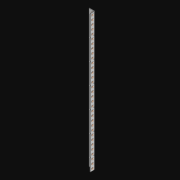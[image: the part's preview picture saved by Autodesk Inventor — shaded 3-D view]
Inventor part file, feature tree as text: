
AUTODESK INVENTOR PART (.ipt)
format: ipt  version: 2021 (Build 250183000, 183)  size: 1,321,984 bytes
history: native  units: in
note: dims shown in document units (in); Inventor stores cm internally (conversion verified against a paired STEP export)
features: extrude x68, other x66, sketch x4, pattern_linear x2, sheet_metal_op x1
ambient origin geometry x8: Origin, YZ Plane, XZ Plane, XY Plane, X Axis, Y Axis, Z Axis, Center Point
bodies: Solid1 (feature_tree)
feature tree (141):
  pattern_linear  "Rectangular Pattern1"  Spacing1=0.5in  [1 undecoded]
  pattern_linear  "Rectangular Pattern3"  Count1=33  [1 undecoded]
  extrude  "Extrusion1"  Depth=0.5in
  extrude  "Extrusion2"  Depth=1.0in
  sketch  "Sketch1"  dims[d0=0.182in]
  other  "Srf1"
  sketch  "Sketch3"  dims[d1=0.063in d2=0.0in]
  other  "Srf3"
  other  "Srf4"
  other  "Srf5"
  other  "Srf6"
  other  "Srf7"
  other  "Srf8"
  other  "Srf9"
  other  "Srf10"
  other  "Srf11"
  other  "Srf12"
  other  "Srf13"
  other  "Srf14"
  other  "Srf15"
  other  "Srf16"
  other  "Srf17"
  other  "Srf18"
  other  "Srf19"
  other  "Srf20"
  other  "Srf21"
  other  "Srf22"
  other  "Srf23"
  other  "Srf24"
  other  "Srf25"
  other  "Srf26"
  other  "Srf27"
  other  "Srf28"
  other  "Srf29"
  other  "Srf30"
  other  "Srf31"
  other  "Srf32"
  other  "Srf33"
  other  "Srf34"
  other  "Srf35"
  other  "Srf142"
  other  "Srf143"
  other  "Srf144"
  other  "Srf145"
  other  "Srf146"
  other  "Srf147"
  other  "Srf148"
  other  "Srf149"
  other  "Srf150"
  other  "Srf151"
  other  "Srf152"
  other  "Srf153"
  other  "Srf154"
  other  "Srf155"
  other  "Srf156"
  other  "Srf157"
  other  "Srf158"
  other  "Srf159"
  other  "Srf160"
  other  "Srf161"
  other  "Srf162"
  other  "Srf163"
  other  "Srf164"
  other  "Srf165"
  other  "Srf166"
  other  "Srf167"
  other  "Srf168"
  other  "Srf169"
  other  "Srf170"
  other  "Srf171"
  other  "Srf172"
  other  "Srf173"
  sketch  "Sketch4"  dims[d6=0.182in]
  sketch  "Sketch5"  dims[d7=0.063in d8=0.0in d11=0.5in d12=0.3937in d14=0.5in d18=12.9921in d20=0.5in d21=1.0in d22=0.0in d23=0.841in d24=0.0in]
  sheet_metal_op  "Fold1"
  extrude  "ExtrusionSrf1"  TaperAngle=0.0deg  [1 undecoded]
  extrude  "ExtrusionSrf3"  Depth=1.0in TaperAngle=0.0deg
  extrude  "ExtrusionSrf4"  [1 undecoded]
  extrude  "ExtrusionSrf5"  [1 undecoded]
  extrude  "ExtrusionSrf6"  [1 undecoded]
  extrude  "ExtrusionSrf7"  [1 undecoded]
  extrude  "ExtrusionSrf8"  [1 undecoded]
  extrude  "ExtrusionSrf9"  [1 undecoded]
  extrude  "ExtrusionSrf10"  [1 undecoded]
  extrude  "ExtrusionSrf11"  [1 undecoded]
  extrude  "ExtrusionSrf12"  [1 undecoded]
  extrude  "ExtrusionSrf13"  [1 undecoded]
  extrude  "ExtrusionSrf14"  [1 undecoded]
  extrude  "ExtrusionSrf15"  [1 undecoded]
  extrude  "ExtrusionSrf16"  [1 undecoded]
  extrude  "ExtrusionSrf17"  [1 undecoded]
  extrude  "ExtrusionSrf18"  [1 undecoded]
  extrude  "ExtrusionSrf19"  [1 undecoded]
  extrude  "ExtrusionSrf20"  [1 undecoded]
  extrude  "ExtrusionSrf21"  [1 undecoded]
  extrude  "ExtrusionSrf22"  [1 undecoded]
  extrude  "ExtrusionSrf23"  [1 undecoded]
  extrude  "ExtrusionSrf24"  [1 undecoded]
  extrude  "ExtrusionSrf25"  [1 undecoded]
  extrude  "ExtrusionSrf26"  [1 undecoded]
  extrude  "ExtrusionSrf27"  [1 undecoded]
  extrude  "ExtrusionSrf28"  [1 undecoded]
  extrude  "ExtrusionSrf29"  [1 undecoded]
  extrude  "ExtrusionSrf30"  [1 undecoded]
  extrude  "ExtrusionSrf31"  [1 undecoded]
  extrude  "ExtrusionSrf32"  [1 undecoded]
  extrude  "ExtrusionSrf33"  [1 undecoded]
  extrude  "ExtrusionSrf34"  [1 undecoded]
  extrude  "ExtrusionSrf35"  [1 undecoded]
  extrude  "ExtrusionSrf142"  [1 undecoded]
  extrude  "ExtrusionSrf143"  [1 undecoded]
  extrude  "ExtrusionSrf144"  [1 undecoded]
  extrude  "ExtrusionSrf145"  [1 undecoded]
  extrude  "ExtrusionSrf146"  [1 undecoded]
  extrude  "ExtrusionSrf147"  [1 undecoded]
  extrude  "ExtrusionSrf148"  [1 undecoded]
  extrude  "ExtrusionSrf149"  [1 undecoded]
  extrude  "ExtrusionSrf150"  [1 undecoded]
  extrude  "ExtrusionSrf151"  [1 undecoded]
  extrude  "ExtrusionSrf152"  [1 undecoded]
  extrude  "ExtrusionSrf153"  [1 undecoded]
  extrude  "ExtrusionSrf154"  [1 undecoded]
  extrude  "ExtrusionSrf155"  [1 undecoded]
  extrude  "ExtrusionSrf156"  [1 undecoded]
  extrude  "ExtrusionSrf157"  [1 undecoded]
  extrude  "ExtrusionSrf158"  [1 undecoded]
  extrude  "ExtrusionSrf159"  [1 undecoded]
  extrude  "ExtrusionSrf160"  [1 undecoded]
  extrude  "ExtrusionSrf161"  [1 undecoded]
  extrude  "ExtrusionSrf162"  [1 undecoded]
  extrude  "ExtrusionSrf163"  [1 undecoded]
  extrude  "ExtrusionSrf164"  [1 undecoded]
  extrude  "ExtrusionSrf165"  [1 undecoded]
  extrude  "ExtrusionSrf166"  [1 undecoded]
  extrude  "ExtrusionSrf167"  [1 undecoded]
  extrude  "ExtrusionSrf168"  [1 undecoded]
  extrude  "ExtrusionSrf169"  [1 undecoded]
  extrude  "ExtrusionSrf170"  [1 undecoded]
  extrude  "ExtrusionSrf171"  [1 undecoded]
  extrude  "ExtrusionSrf172"  [1 undecoded]
  extrude  "ExtrusionSrf173"  [1 undecoded]
note: 67 required parameter values undecoded (feature->parameter linkage not recoverable at this tier; creation-order binding heuristic only, values carry confidence <= 0.55)
